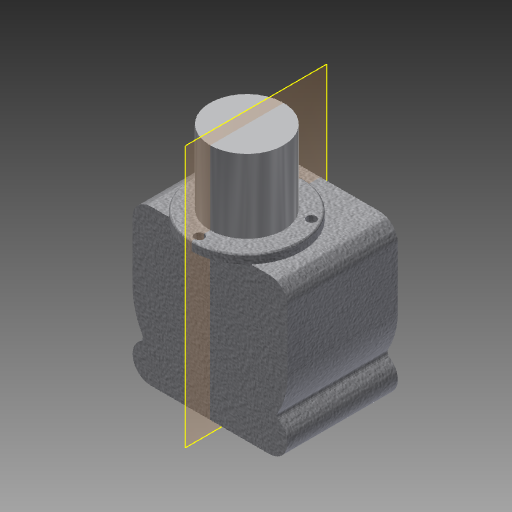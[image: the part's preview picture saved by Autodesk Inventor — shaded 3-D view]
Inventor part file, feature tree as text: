
AUTODESK INVENTOR PART (.ipt)
format: ipt  version: 2017.1 (Build 211199000, 199)  size: 265,216 bytes
history: native  units: in
note: dims shown in document units (in); Inventor stores cm internally (conversion verified against a paired STEP export)
features: sketch x5, extrude x4, fillet x3, reference x3, projected_geometry x2, hole x1
ambient origin geometry x8: Origin, YZ Plane, XZ Plane, XY Plane, X Axis, Y Axis, Z Axis, Center Point
bodies: Solid1 (feature_tree)
feature tree (18):
  extrude  "Extrusion1"  Depth=2.11in
  fillet  "Fillet1"  Radius=1.5in
  extrude  "Extrusion2"  Depth=0.5in
  fillet  "Fillet2"  Radius=0.5in
  extrude  "Extrusion3"  Depth=1.055in
  fillet  "Fillet3"  Radius=1.0in
  extrude  "Extrusion4"  Depth=1.5in
  hole  "Hole1"  [1 undecoded]
  sketch  "Sketch1"  dims[d0=2.11in d1=2.11in d2=1.5in d3=0.0in]
  sketch  "Sketch3"  dims[d4=0.25in d8=2.0in d9=0.5in]
  sketch  "Sketch4"  dims[d10=0.5in d12=1.055in d13=1.0in d14=0.0in]
  projected_geometry  "Projected Loop1"
  projected_geometry  "Projected Loop2"
  sketch  "Sketch5"  dims[d15=0.0625in d16=1.5in]
  sketch  "Sketch6"  dims[d17=0.25in d18=0.125in d19=0.0in d20=0.0312in d22=1.0in d23=0.0in d24=0.25in d25=0.129in d26=0.75in d27=0.225in d28=0.25in d29=0.5635in d30=0.25in d31=0.8108in]
  reference  "Reference1"
  reference  "Reference2"
  reference  "Reference3"
note: 1 required parameter value undecoded (feature->parameter linkage not recoverable at this tier; creation-order binding heuristic only, values carry confidence <= 0.55)
